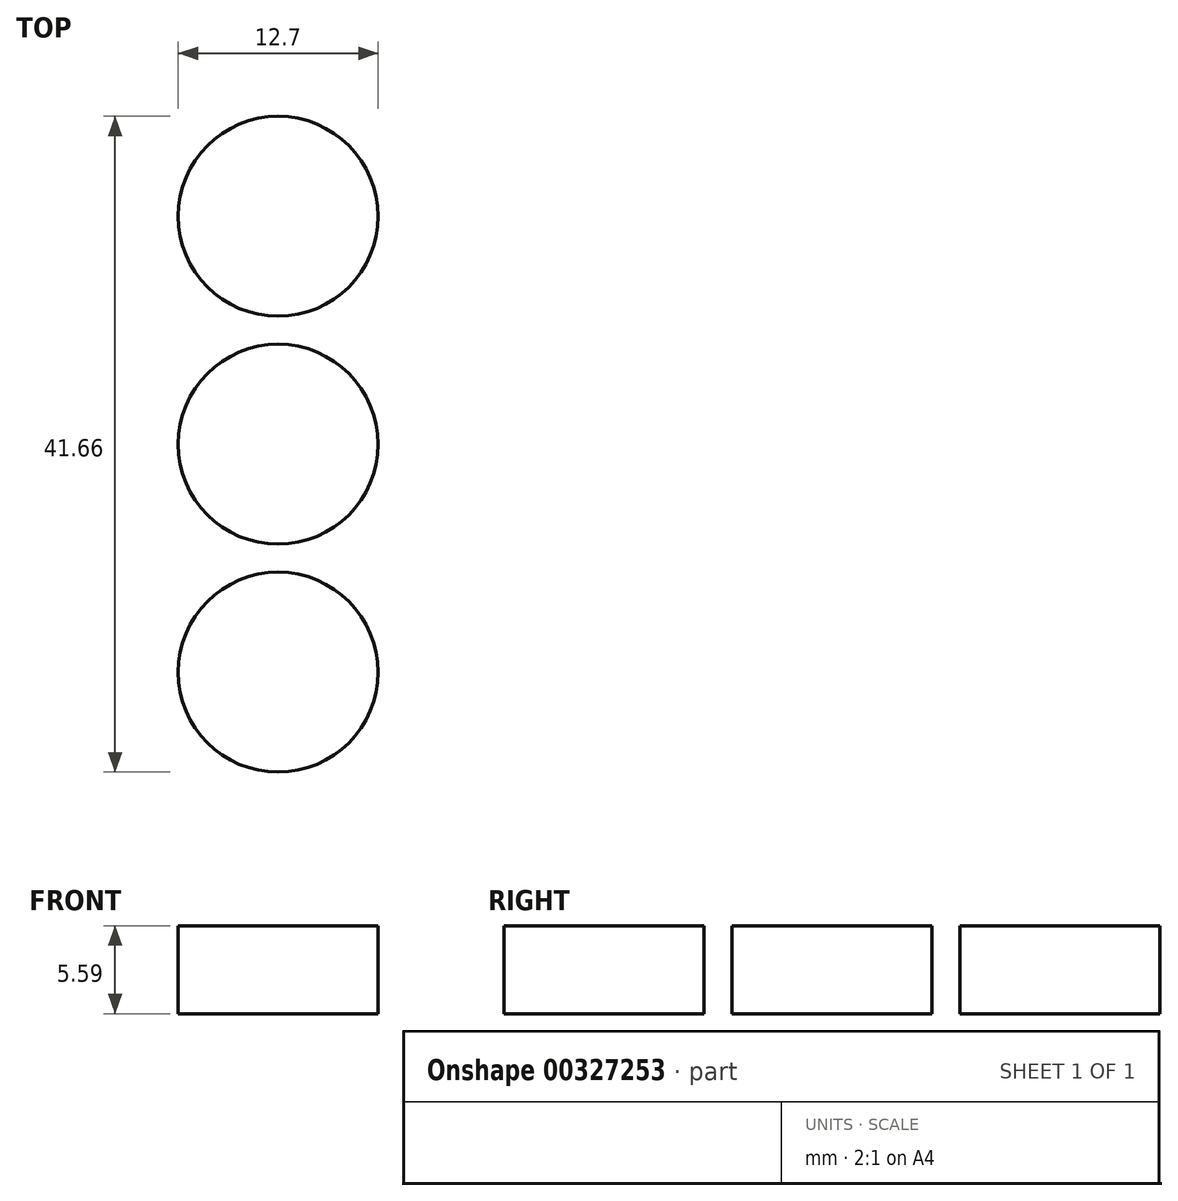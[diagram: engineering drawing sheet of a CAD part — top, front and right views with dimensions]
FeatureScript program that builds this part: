
annotation { "Feature Type Name" : "Feature", "Feature Type Description" : "" }
export const myFeature = defineFeature(function(context is Context, id is Id, definition is map)
    precondition{}
    {
        {
            var Q0;
            Q0=qCreatedBy(makeId("Top.planeOp"),FACE);
            var sketch = newSketch(context, id + "F0", { "sketchPlane" : qUnion([Q0])});
            skCircle(sketch, "E0", {"center": v(0, 0) * mm, "radius": 6.35 * mm});
            skSolve(sketch);
        }
        {
            var Q0;
            Q0=makeQuery(id+"F0.imprint","IMPRINT",FACE,{"disambiguationData":[TD([[makeQuery(id+"F0.imprint","IMPRINT",EDGE,{"derivedFrom":sQuery(id+"F0.wireOp",EDGE,"E0")}),1.0]])]});
            extrude(context, id + "F1", {"entities" : qUnion([Q0]), "depth" : 5.6 * mm});
        }
        {
            var Q0;
            Q0=makeQuery(id+"F1.opExtrude","SWEPT_BODY",BODY,{"disambiguationData":[OSD([sQuery(id+"F0.wireOp",EDGE,"E0")])]});
            transform(context, id + "F2", {"entities" : qUnion([Q0]), "transformType" : TransformType.TRANSLATION_3D, "dx" : 0 * mm, "dy" : -14.48 * mm, "dz" : 0 * mm, "makeCopy" : true});
        }
        {
            var Q0;
            Q0=makeQuery(id+"F2.opPattern","COPY",BODY,{"derivedFrom":makeQuery(id+"F1.opExtrude","SWEPT_BODY",BODY,{"disambiguationData":[OSD([sQuery(id+"F0.wireOp",EDGE,"E0")])]}),"instanceName":"1"});
            var Q1;
            Q1=qCreatedBy(makeId("Front.planeOp"),FACE);
            mirror(context, id + "F3", {"entities" : qUnion([Q0]), "mirrorPlane" : qUnion([Q1])});
        }
    });
